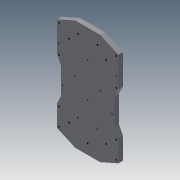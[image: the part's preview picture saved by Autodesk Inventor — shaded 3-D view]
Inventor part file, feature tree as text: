
AUTODESK INVENTOR PART (.ipt)
format: ipt  version: 2013 (Build 170138000, 138)  size: 280,064 bytes
history: native  units: mm
features: extrude x5, sketch x5
ambient origin geometry x8: Origin, YZ Plane, XZ Plane, XY Plane, X Axis, Y Axis, Z Axis, Center Point
bodies: Solid1 (feature_tree)
feature tree (10):
  extrude  "Extrusion1"  Depth=4.0mm
  extrude  "Extrusion2"  Depth=4.0mm
  extrude  "Extrusion3"  Depth=4.0mm
  extrude  "Extrusion4"  Depth=4.0mm
  extrude  "Extrusion5"  Depth=4.0mm
  sketch  "Sketch1"  dims[d0=4.0mm d1=4.0mm]
  sketch  "Sketch2"  dims[d2=4.0mm d3=4.0mm]
  sketch  "Sketch3"  dims[d4=4.0mm d5=4.0mm]
  sketch  "Sketch4"  dims[d6=4.0mm d7=4.0mm]
  sketch  "Sketch5"  dims[d8=4.0mm d9=4.0mm d10=4.0mm d11=4.0mm d12=4.0mm d13=4.0mm d14=4.0mm d15=4.0mm d16=4.0mm d17=4.0mm d18=4.0mm d19=4.0mm d20=4.0mm d21=4.0mm d22=4.0mm d23=4.0mm d24=4.0mm d25=2.0mm d26=0.0mm d27=1.3mm d28=0.0mm d29=8.0mm d30=0.0mm d31=10.0mm d32=0.0mm d33=10.0mm d34=0.0mm]
